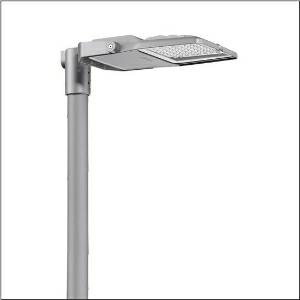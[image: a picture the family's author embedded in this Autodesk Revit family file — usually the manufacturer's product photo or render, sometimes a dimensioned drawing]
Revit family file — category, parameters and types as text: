
# Revit family: floodlight_fl_21_iq_mini___pl64_5xa7771b2e3a_ab64
name_source: partatom
category: Lighting Fixtures
units: mm (PartAtom-declared; Revit-internal decimal feet)

## family parameters
Cut with Voids When Loaded = No
Host = Face
Light Source = No
Part Type = Normal
Room Calculation Point = No
Round Connector Dimension = Use Diameter
Shared = No

## types (1)
- --- (1 x LED, 6020 lm, 45.5 W, 3000K)
    Apparent Load = 46 VA
    CIE Flux Codes = 28 80 98 100 100
    Color Rendering = 70
    Color Temperature = 3000K
    Default Elevation = 1800 mm
    Description = Floodlight FL 21 iQ mini, floodlight, primary light control with lens, of PMMA, primary optical cover: protective disc, of toughened safety glass, transparent, light distribution: PL64, light emission: direct distribution, installation type: surface-mounted, LED, High Power LED, rated luminous flux: 6.020lm, luminous efficacy: 132lm/W, light colour: 730, colour temperature: 3000K, control gear: iQ Comfort/DALI, control: Auto-Match, Temp-Guard, Lumen-Switch, Night-Set, Smart-Wire, Light-Fading, Desk-Remote (wireless, voltage-free reading and setting of iQ features in the workshop via application-optimized NFC function/RFID function), optimised constant luminous flux control (CLO 2.0), with terminal, 6-pole, mains connection: 220..240V, AC, 50/60Hz, start of lifetime: 46W, end of service life: 48W, reduction: 22W, luminaire housing, of diecast aluminium, powder-coated, Siteco® metallic grey (DB 702S), corrosivity category C5 mid according to DIN EN ISO 12944, suitable for swimming pools, chlorine-resistant, sealing non-destructively replaceable, please order mast flange separately, mast bracket, of steel, galvanised, powder-coated, Siteco® metallic grey (DB 702S), protection rating (complete): IP66, insulation class (complete): insulation class II (safety insulation), certification: CE, ENEC, VDE, protection symbol: D, impact resistance: IK08, permissible operating ambient temperature: -40..+40°C, permissible operating ambient temperature for outdoor applications: -40..+50°C, standard: DIN EN 12944, LABS conformity tested according to VDMA 24364:2018-05, packaging unit: 1 piece

Light Distribution: PL64
    Height = 70 mm
    Lamp = 1 x LED
    Lamp Light Flux = 6020 lm
    Lamp Power = 45.5 W
    Lamp count = 1
    Length = 485 mm
    Luminous efficacy = 132 lm/W
    Manufacturer = Siteco
    ModVariant = No
    Model = 5XA7771B2E3A
    Number of Poles = 1
    OnlyDefault = Yes
    Power Factor = 1
    Product Name = Floodlight FL 21 iQ mini | PL64
    Product group = floodlight | pylon annexe
    ProductGroupID = 6201
    Protection Class = Protection class II
    Protection Degree = IP 66
    RLX_Detail_Level = 1
    RLX_Emergency_Light_Flux = 0 lm
    RLX_Emergency_Type = 0
    RLX_Emergency_Type_DB = No
    RlxData = <blob elided: 101257 chars, md5=237a6bba>
    Socket = socket
    Standby Power = 0 W
    System Light Flux = 6020 lm
    System Power = 46 W
    Type Comments = factory setting: luminous flux: 100 % | dim-lin: 254 | 463 mA
    Type Image = l_1007125.jpg
    URL = http://relux.com
    VarID = @adj_188619
    Voltage = 0 V
    Weight = 0.00 kg
    Width = 337 mm

## geometry (parser evidence)
native form markers: Blend x4, Sweep x13
no freeform markers — native parametric forms only
